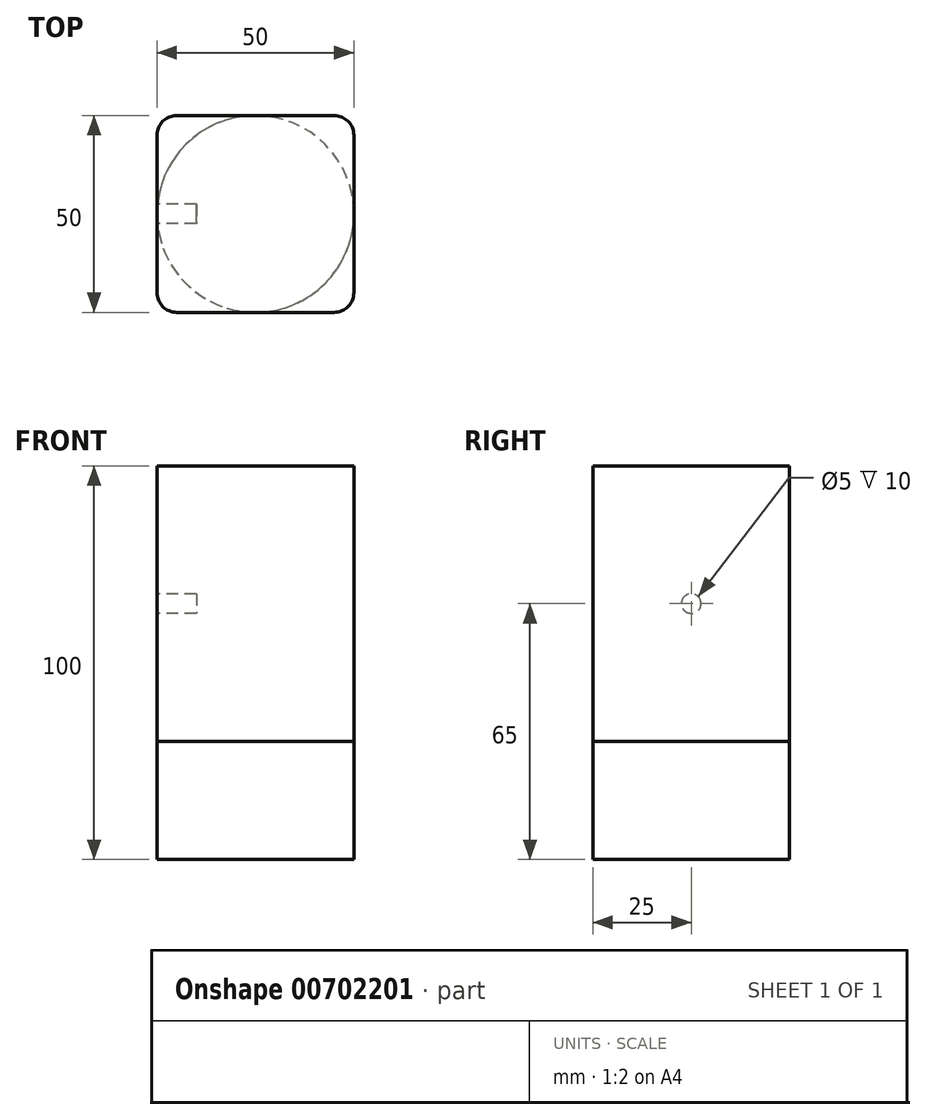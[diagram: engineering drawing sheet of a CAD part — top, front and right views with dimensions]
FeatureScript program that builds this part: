
annotation { "Feature Type Name" : "Feature", "Feature Type Description" : "" }
export const myFeature = defineFeature(function(context is Context, id is Id, definition is map)
    precondition{}
    {
        {
            var Q0;
            Q0=qCreatedBy(makeId("Front.planeOp"),FACE);
            var sketch = newSketch(context, id + "F0", { "sketchPlane" : qUnion([Q0])});
            skLineSegment(sketch, "E0.bottom", {"start": v(25, -35) * mm, "end": v(-25, -35) * mm});
            skLineSegment(sketch, "E0.top", {"start": v(25, 35) * mm, "end": v(-25, 35) * mm});
            skLineSegment(sketch, "E0.left", {"start": v(25, -35) * mm, "end": v(25, 35) * mm});
            skLineSegment(sketch, "E0.right", {"start": v(-25, -35) * mm, "end": v(-25, 35) * mm});
            skPoint(sketch, "E0.middle", {"position": v(0, 0) * mm});
            skSolve(sketch);
        }
        {
            var Q0;
            Q0=makeQuery(id+"F0.imprint","IMPRINT",FACE,{"disambiguationData":[TD([[makeQuery(id+"F0.imprint","IMPRINT",EDGE,{"derivedFrom":sQuery(id+"F0.wireOp",EDGE,"E0.bottom")}),-1.0]])]});
            extrude(context, id + "F1", {"entities" : qUnion([Q0]), "endBound" : BoundingType.SYMMETRIC, "depth" : 50 * mm, "offsetDistance" : 25 * mm});
        }
        {
            var Q0;
            Q0=makeQuery(id+"F1.opExtrude","SWEPT_FACE",FACE,{"disambiguationData":[OSD([sQuery(id+"F0.wireOp",EDGE,"E0.bottom")])]});
            var sketch = newSketch(context, id + "F2", { "sketchPlane" : qUnion([Q0])});
            skCircle(sketch, "E1", {"center": v(0, 0) * mm, "radius": 25 * mm});
            skSolve(sketch);
        }
        {
            var Q0;
            Q0 = qSketchRegion(id + "F2", true);
            extrude(context, id + "F3", {"entities" : qUnion([Q0]), "operationType" : NewBodyOperationType.ADD, "depth" : 30 * mm, "offsetDistance" : 25 * mm});
        }
        {
            var Q0;
            Q0=makeQuery(id+"F1.opExtrude","CAP_EDGE",EDGE,{"disambiguationData":[OSD([sQuery(id+"F0.wireOp",EDGE,"E0.left")])],"isStart":false});
            var Q1;
            Q1=makeQuery(id+"F1.opExtrude","CAP_EDGE",EDGE,{"disambiguationData":[OSD([sQuery(id+"F0.wireOp",EDGE,"E0.right")])],"isStart":false});
            var Q2;
            Q2=makeQuery(id+"F1.opExtrude","CAP_EDGE",EDGE,{"disambiguationData":[OSD([sQuery(id+"F0.wireOp",EDGE,"E0.right")])],"isStart":true});
            var Q3;
            Q3=makeQuery(id+"F1.opExtrude","CAP_EDGE",EDGE,{"disambiguationData":[OSD([sQuery(id+"F0.wireOp",EDGE,"E0.left")])],"isStart":true});
            fillet(context, id + "F4", {"entities" : qUnion([Q0, Q1, Q2, Q3]), "radius" : 5 * mm, "tangentPropagation" : true, "allowEdgeOverflow" : false});
        }
        {
            var Q0;
            Q0=makeQuery(id+"F1.opExtrude","SWEPT_FACE",FACE,{"disambiguationData":[OSD([sQuery(id+"F0.wireOp",EDGE,"E0.right")])]});
            var sketch = newSketch(context, id + "F5", { "sketchPlane" : qUnion([Q0])});
            skCircle(sketch, "E2", {"center": v(0, 0) * mm, "radius": 2.5 * mm});
            skSolve(sketch);
        }
        {
            var Q0;
            Q0=makeQuery(id+"F5.imprint","IMPRINT",FACE,{"disambiguationData":[TD([[makeQuery(id+"F5.imprint","IMPRINT",EDGE,{"derivedFrom":sQuery(id+"F5.wireOp",EDGE,"E2")}),1.0]])]});
            extrude(context, id + "F6", {"entities" : qUnion([Q0]), "operationType" : NewBodyOperationType.REMOVE, "oppositeDirection" : true, "depth" : 10 * mm, "offsetDistance" : 25 * mm});
        }
    });
